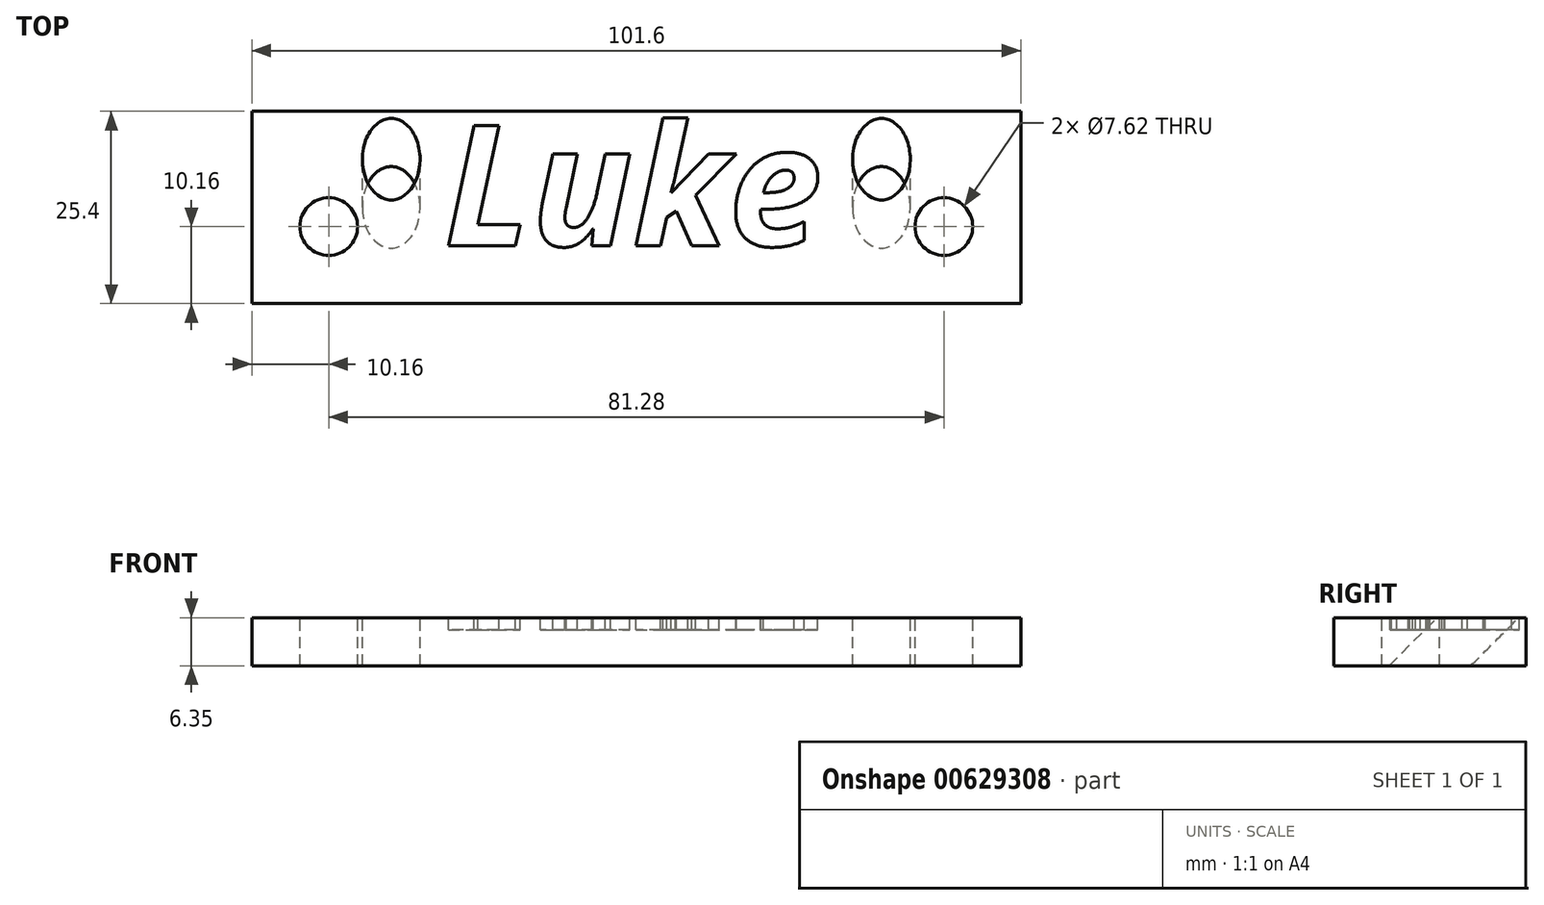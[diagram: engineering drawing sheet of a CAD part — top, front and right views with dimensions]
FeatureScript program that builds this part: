
annotation { "Feature Type Name" : "Feature", "Feature Type Description" : "" }
export const myFeature = defineFeature(function(context is Context, id is Id, definition is map)
    precondition{}
    {
        {
            var Q0;
            Q0=qCreatedBy(makeId("Top.planeOp"),FACE);
            var sketch = newSketch(context, id + "F0", { "sketchPlane" : qUnion([Q0])});
            skLineSegment(sketch, "E0.bottom", {"start": v(-50.8, -12.7) * mm, "end": v(50.8, -12.7) * mm});
            skLineSegment(sketch, "E0.top", {"start": v(-50.8, 12.7) * mm, "end": v(50.8, 12.7) * mm});
            skLineSegment(sketch, "E0.left", {"start": v(-50.8, -12.7) * mm, "end": v(-50.8, 12.7) * mm});
            skLineSegment(sketch, "E0.right", {"start": v(50.8, -12.7) * mm, "end": v(50.8, 12.7) * mm});
            skSolve(sketch);
        }
        {
            var Q0;
            Q0 = qSketchRegion(id + "F0", true);
            extrude(context, id + "F1", {"entities" : qUnion([Q0]), "depth" : 6.35 * mm, "offsetDistance" : 25.4 * mm});
        }
        {
            var Q0;
            Q0=makeQuery(id+"F1.opExtrude","CAP_FACE",FACE,{"disambiguationData":[OSD([sQuery(id+"F0.wireOp",EDGE,"E0.bottom"),sQuery(id+"F0.wireOp",EDGE,"E0.top"),sQuery(id+"F0.wireOp",EDGE,"E0.left"),sQuery(id+"F0.wireOp",EDGE,"E0.right")])],"isStart":false});
            var sketch = newSketch(context, id + "F2", { "sketchPlane" : qUnion([Q0])});
            skCircle(sketch, "E1", {"center": v(-40.64, -2.54) * mm, "radius": 3.81 * mm});
            skCircle(sketch, "E2", {"center": v(40.64, -2.54) * mm, "radius": 3.81 * mm});
            skSolve(sketch);
        }
        {
            var Q0;
            Q0=makeQuery(id+"F2.imprint","IMPRINT",FACE,{"disambiguationData":[TD([[makeQuery(id+"F2.imprint","IMPRINT",EDGE,{"derivedFrom":sQuery(id+"F2.wireOp",EDGE,"E1")}),1.0]])]});
            var Q1;
            Q1=makeQuery(id+"F2.imprint","IMPRINT",FACE,{"disambiguationData":[TD([[makeQuery(id+"F2.imprint","IMPRINT",EDGE,{"derivedFrom":sQuery(id+"F2.wireOp",EDGE,"E2")}),1.0]])]});
            extrude(context, id + "F3", {"entities" : qUnion([Q0, Q1]), "operationType" : NewBodyOperationType.REMOVE, "oppositeDirection" : true, "depth" : 25.4 * mm, "offsetDistance" : 25.4 * mm});
        }
        {
            var Q0;
            Q0=qCreatedBy(makeId("Front.planeOp"),FACE);
            var sketch = newSketch(context, id + "F4", { "sketchPlane" : qUnion([Q0])});
            skPoint(sketch, "E3", {"position": v(-76.2, 76.2) * mm});
            skPoint(sketch, "E4.MirrorP", {"position": v(76.2, 76.2) * mm});
            skSolve(sketch);
        }
        {
            var Q0;
            Q0=qCreatedBy(makeId("Top.planeOp"),FACE);
            var sketch = newSketch(context, id + "F5", { "sketchPlane" : qUnion([Q0])});
            skPoint(sketch, "E5", {"position": v(0, 76.2) * mm});
            skSolve(sketch);
        }
        {
            var Q0;
            Q0=sQuery(id+"F5.wireOp",VERTEX,"E5");
            var Q1;
            Q1=sQuery(id+"F4.wireOp",VERTEX,"E3");
            var Q2;
            Q2=sQuery(id+"F4.wireOp",VERTEX,"E4.MirrorP");
            cPlane(context, id + "F6", {"entities" : qUnion([Q0, Q1, Q2]), "cplaneType" : CPlaneType.THREE_POINT, "offset" : 25.4 * mm, "width" : 152.4 * mm, "height" : 152.4 * mm});
        }
        {
            var Q0;
            Q0=qCreatedBy(id+"F6.planeOp",FACE);
            var sketch = newSketch(context, id + "F7", { "sketchPlane" : qUnion([Q0])});
            skCircle(sketch, "E6", {"center": v(-32.39, 0) * mm, "radius": 3.81 * mm});
            skCircle(sketch, "E7", {"center": v(32.39, 0) * mm, "radius": 3.81 * mm});
            skSolve(sketch);
        }
        {
            var Q0;
            Q0=makeQuery(id+"F7.imprint","IMPRINT",FACE,{"disambiguationData":[TD([[makeQuery(id+"F7.imprint","IMPRINT",EDGE,{"derivedFrom":sQuery(id+"F7.wireOp",EDGE,"E6")}),1.0]])]});
            var Q1;
            Q1=makeQuery(id+"F7.imprint","IMPRINT",FACE,{"disambiguationData":[TD([[makeQuery(id+"F7.imprint","IMPRINT",EDGE,{"derivedFrom":sQuery(id+"F7.wireOp",EDGE,"E7")}),1.0]])]});
            extrude(context, id + "F8", {"entities" : qUnion([Q0, Q1]), "operationType" : NewBodyOperationType.REMOVE, "endBound" : BoundingType.THROUGH_ALL, "depth" : 25.4 * mm, "offsetDistance" : 25.4 * mm});
        }
        {
            var Q0;
            Q0=makeQuery(id+"F1.opExtrude","CAP_FACE",FACE,{"disambiguationData":[OSD([sQuery(id+"F0.wireOp",EDGE,"E0.bottom"),sQuery(id+"F0.wireOp",EDGE,"E0.top"),sQuery(id+"F0.wireOp",EDGE,"E0.left"),sQuery(id+"F0.wireOp",EDGE,"E0.right")])],"isStart":false});
            var sketch = newSketch(context, id + "F9", { "sketchPlane" : qUnion([Q0])});
            skText(sketch, "E8", { "text": "Luke", "fontName": "OpenSans-BoldItalic.ttf"});
            const initialGuessF9  = {"E8": [-0.0254, -0.00508, 1, 0, 0.016]};
            skSetInitialGuess(sketch, initialGuessF9);
            skSolve(sketch);
        }
        {
            var Q0;
            Q0 = qSketchRegion(id + "F9", true);
            extrude(context, id + "F10", {"entities" : qUnion([Q0]), "operationType" : NewBodyOperationType.REMOVE, "oppositeDirection" : true, "depth" : 1.59 * mm, "offsetDistance" : 25.4 * mm});
        }
    });
